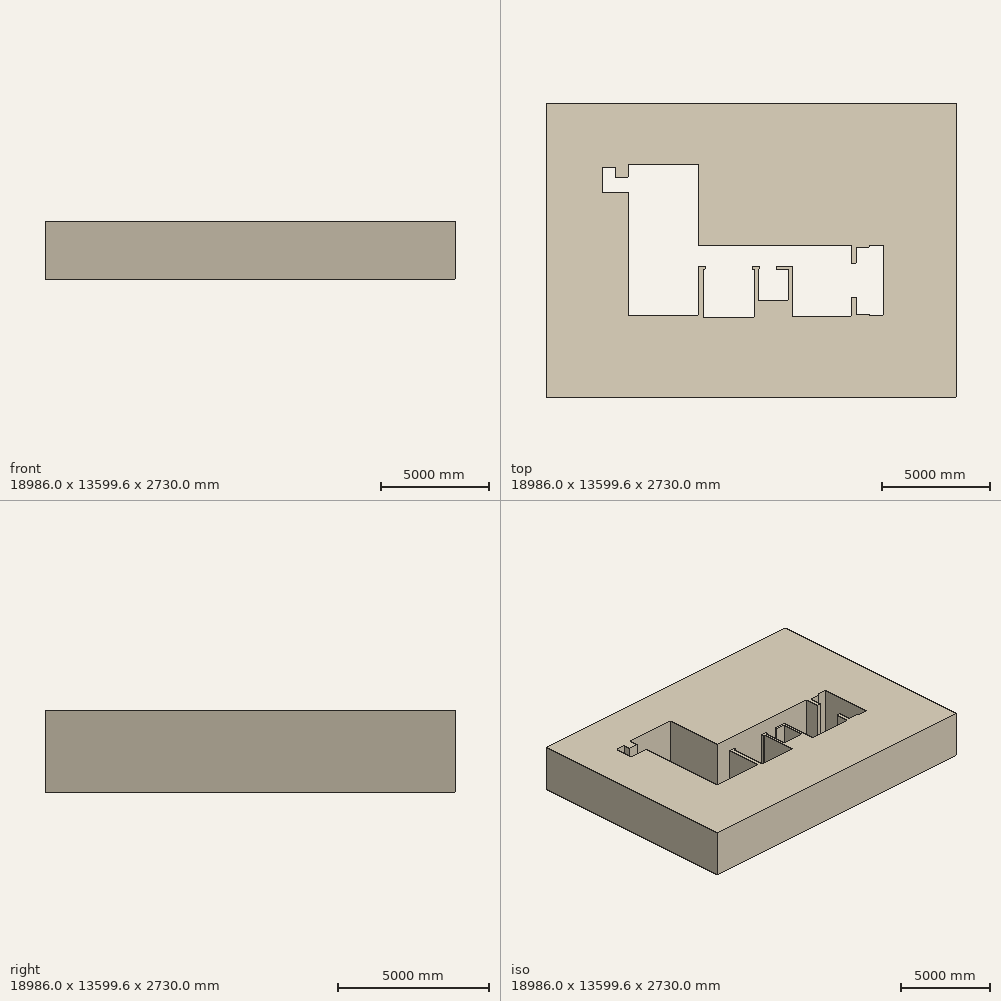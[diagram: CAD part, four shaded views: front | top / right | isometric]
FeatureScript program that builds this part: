
annotation { "Feature Type Name" : "Feature", "Feature Type Description" : "" }
export const myFeature = defineFeature(function(context is Context, id is Id, definition is map)
    precondition{}
    {
        {
            var Q0;
            Q0=qCreatedBy(makeId("Top.planeOp"),FACE);
            var sketch = newSketch(context, id + "F0", { "sketchPlane" : qUnion([Q0])});
            skLineSegment(sketch, "E0", {"start": v(6598.23, 1419.62) * mm, "end": v(6598.23, 569.62) * mm});
            skLineSegment(sketch, "E1", {"start": v(6598.23, 569.62) * mm, "end": v(6838.23, 569.62) * mm});
            skLineSegment(sketch, "E2", {"start": v(6838.23, 569.62) * mm, "end": v(6838.23, 1319.62) * mm});
            skLineSegment(sketch, "E3", {"start": v(6838.23, 1319.62) * mm, "end": v(7438.23, 1319.62) * mm});
            skLineSegment(sketch, "E4", {"start": v(7438.23, 1319.62) * mm, "end": v(7438.23, 1409.62) * mm});
            skLineSegment(sketch, "E5", {"start": v(7438.23, 1409.62) * mm, "end": v(8088.23, 1409.62) * mm});
            skLineSegment(sketch, "E6", {"start": v(8088.23, 1409.62) * mm, "end": v(8088.23, -1840.38) * mm});
            skLineSegment(sketch, "E7", {"start": v(8088.23, -1840.38) * mm, "end": v(7438.23, -1840.38) * mm});
            skLineSegment(sketch, "E8", {"start": v(7438.23, -1840.38) * mm, "end": v(7438.23, -1750.38) * mm});
            skLineSegment(sketch, "E9", {"start": v(7438.23, -1750.38) * mm, "end": v(6838.23, -1750.38) * mm});
            skLineSegment(sketch, "E10", {"start": v(6838.23, -1750.38) * mm, "end": v(6838.23, -1000.38) * mm});
            skLineSegment(sketch, "E11", {"start": v(6838.23, -1000.38) * mm, "end": v(6598.23, -1000.38) * mm});
            skLineSegment(sketch, "E12", {"start": v(6598.23, -1000.38) * mm, "end": v(6598.23, -1850.38) * mm});
            skLineSegment(sketch, "E13", {"start": v(6598.23, -1850.38) * mm, "end": v(3853.23, -1850.38) * mm});
            skLineSegment(sketch, "E14", {"start": v(3853.23, -1850.38) * mm, "end": v(3853.23, 449.62) * mm});
            skLineSegment(sketch, "E15", {"start": v(3853.23, 449.62) * mm, "end": v(3113.23, 449.62) * mm});
            skLineSegment(sketch, "E16", {"start": v(3113.23, 449.62) * mm, "end": v(3113.23, 309.62) * mm});
            skLineSegment(sketch, "E17", {"start": v(3113.23, 309.62) * mm, "end": v(3693.23, 309.62) * mm});
            skLineSegment(sketch, "E18", {"start": v(2293.23, -1120.38) * mm, "end": v(2293.23, 309.62) * mm});
            skLineSegment(sketch, "E19", {"start": v(2293.23, 309.62) * mm, "end": v(2363.23, 309.62) * mm});
            skLineSegment(sketch, "E20", {"start": v(2363.23, 309.62) * mm, "end": v(2363.23, 449.62) * mm});
            skLineSegment(sketch, "E21", {"start": v(2363.23, 449.62) * mm, "end": v(2013.23, 449.62) * mm});
            skLineSegment(sketch, "E22", {"start": v(2013.23, 449.62) * mm, "end": v(2013.23, 309.62) * mm});
            skLineSegment(sketch, "E23", {"start": v(2013.23, 309.62) * mm, "end": v(2113.23, 309.62) * mm});
            skLineSegment(sketch, "E24", {"start": v(2113.23, 309.62) * mm, "end": v(2113.23, -1895.38) * mm});
            skLineSegment(sketch, "E25", {"start": v(2113.23, -1895.38) * mm, "end": v(-246.77, -1895.38) * mm});
            skLineSegment(sketch, "E26", {"start": v(-246.77, -1895.38) * mm, "end": v(-246.77, 309.62) * mm});
            skLineSegment(sketch, "E27", {"start": v(-246.77, 309.62) * mm, "end": v(-146.77, 309.62) * mm});
            skLineSegment(sketch, "E28", {"start": v(-146.77, 309.62) * mm, "end": v(-146.77, 449.62) * mm});
            skLineSegment(sketch, "E29", {"start": v(-146.77, 449.62) * mm, "end": v(-486.77, 449.62) * mm});
            skLineSegment(sketch, "E30", {"start": v(-486.77, 449.62) * mm, "end": v(-486.77, -1800.38) * mm});
            skLineSegment(sketch, "E31", {"start": v(2293.23, -1120.38) * mm, "end": v(3693.23, -1120.38) * mm});
            skLineSegment(sketch, "E32", {"start": v(3693.23, -1120.38) * mm, "end": v(3693.23, 309.62) * mm});
            skLineSegment(sketch, "E33", {"start": v(3853.23, 1419.62) * mm, "end": v(6598.23, 1419.62) * mm});
            skLineSegment(sketch, "E34", {"start": v(3853.23, 1419.62) * mm, "end": v(-486.77, 1419.62) * mm});
            skLineSegment(sketch, "E35", {"start": v(-486.77, 1419.62) * mm, "end": v(-486.77, 5179.62) * mm});
            skLineSegment(sketch, "E36", {"start": v(-486.77, 5179.62) * mm, "end": v(-3716.77, 5179.62) * mm});
            skLineSegment(sketch, "E37", {"start": v(-3716.77, 5179.62) * mm, "end": v(-3716.77, 4589.62) * mm});
            skLineSegment(sketch, "E38", {"start": v(-3716.77, 4589.62) * mm, "end": v(-4306.77, 4589.62) * mm});
            skLineSegment(sketch, "E39", {"start": v(-4306.77, 4589.62) * mm, "end": v(-4306.77, 5034.62) * mm});
            skLineSegment(sketch, "E40", {"start": v(-4306.77, 5034.62) * mm, "end": v(-4906.77, 5034.62) * mm});
            skLineSegment(sketch, "E41", {"start": v(-4906.77, 5034.62) * mm, "end": v(-4906.77, 3869.62) * mm});
            skLineSegment(sketch, "E42", {"start": v(-4906.77, 3869.62) * mm, "end": v(-3716.77, 3869.62) * mm});
            skLineSegment(sketch, "E43", {"start": v(-3716.77, 3869.62) * mm, "end": v(-3716.77, -1800.38) * mm});
            skLineSegment(sketch, "E44", {"start": v(-3716.77, -1800.38) * mm, "end": v(-486.77, -1800.38) * mm});
            skLineSegment(sketch, "E45.bottom", {"start": v(-7518.84, 7991.5) * mm, "end": v(11467.13, 7991.5) * mm});
            skLineSegment(sketch, "E45.top", {"start": v(-7518.84, -5608.05) * mm, "end": v(11467.13, -5608.05) * mm});
            skLineSegment(sketch, "E45.left", {"start": v(-7518.84, 7991.5) * mm, "end": v(-7518.84, -5608.05) * mm});
            skLineSegment(sketch, "E45.right", {"start": v(11467.13, 7991.5) * mm, "end": v(11467.13, -5608.05) * mm});
            skSolve(sketch);
        }
        {
            var Q0;
            Q0 = qSketchRegion(id + "F0", true);
            extrude(context, id + "F1", {"entities" : qUnion([Q0]), "depth" : 2730 * mm});
        }
    });
